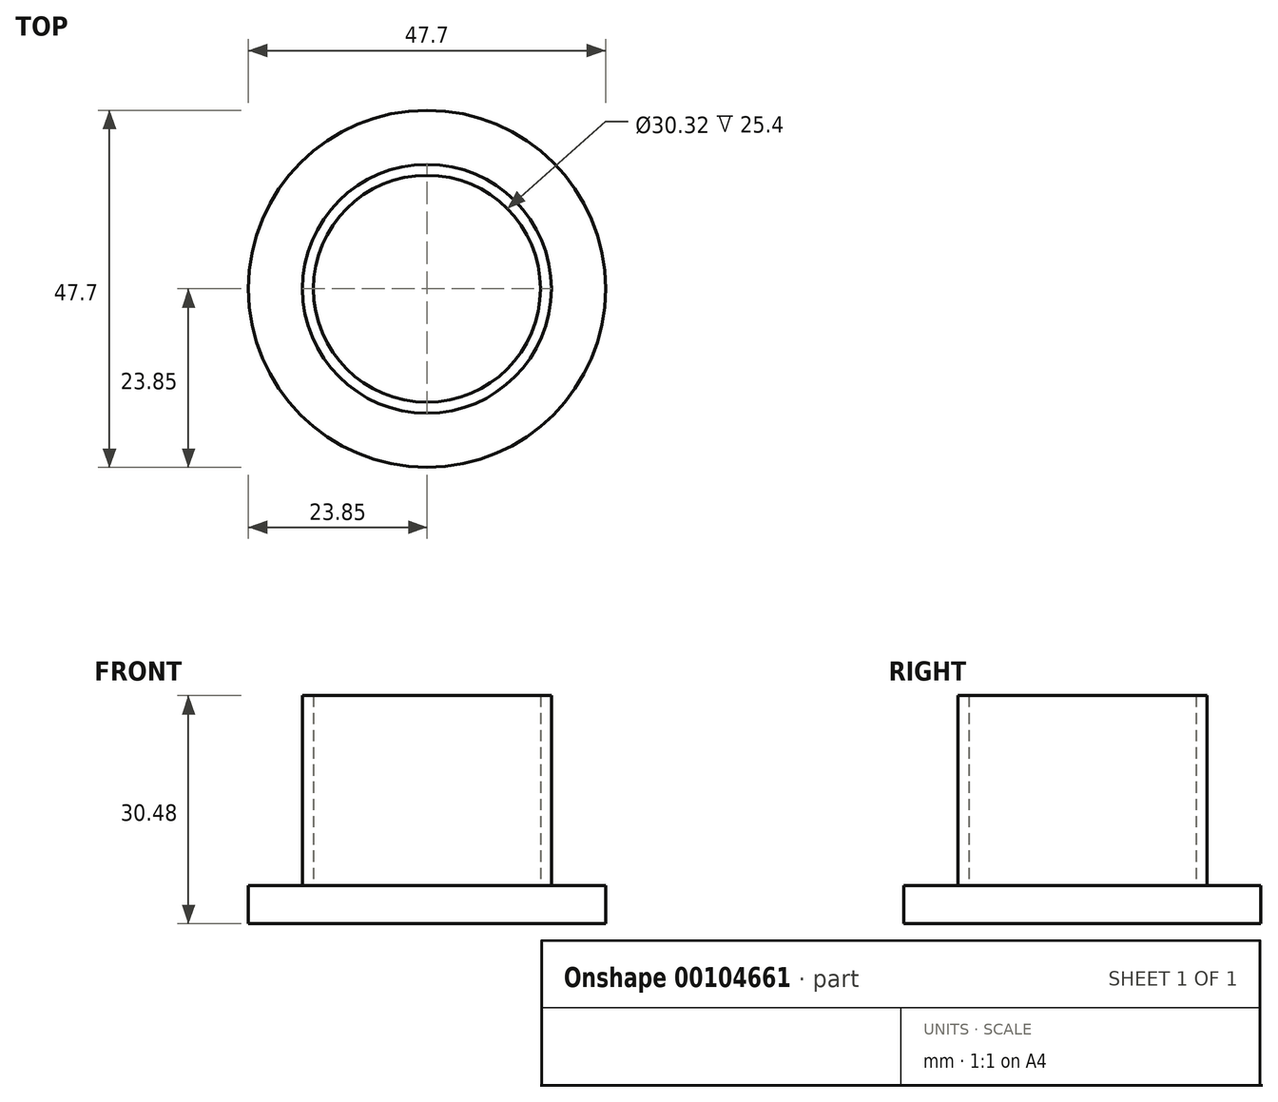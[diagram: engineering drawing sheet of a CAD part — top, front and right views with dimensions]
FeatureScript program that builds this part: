
annotation { "Feature Type Name" : "Feature", "Feature Type Description" : "" }
export const myFeature = defineFeature(function(context is Context, id is Id, definition is map)
    precondition{}
    {
        {
            var Q0;
            Q0=qCreatedBy(makeId("Top.planeOp"),FACE);
            var sketch = newSketch(context, id + "F0", { "sketchPlane" : qUnion([Q0])});
            skCircle(sketch, "E0", {"center": v(0, 0) * mm, "radius": 15.16 * mm});
            skCircle(sketch, "E1", {"center": v(0, 0) * mm, "radius": 16.63 * mm});
            skSolve(sketch);
        }
        {
            var Q0;
            Q0 = qSketchRegion(id + "F0", true);
            extrude(context, id + "F1", {"entities" : qUnion([Q0]), "depth" : 25.4 * mm});
        }
        {
            var Q0;
            Q0=qCreatedBy(makeId("Top.planeOp"),FACE);
            var sketch = newSketch(context, id + "F2", { "sketchPlane" : qUnion([Q0])});
            skCircle(sketch, "E2", {"center": v(0, 0) * mm, "radius": 23.85 * mm});
            skSolve(sketch);
        }
        {
            var Q0;
            Q0=makeQuery(id+"F2.imprint","IMPRINT",FACE,{"disambiguationData":[TD([[makeQuery(id+"F2.imprint","IMPRINT",EDGE,{"derivedFrom":sQuery(id+"F2.wireOp",EDGE,"E2")}),1.0]])]});
            extrude(context, id + "F3", {"entities" : qUnion([Q0]), "operationType" : NewBodyOperationType.ADD, "oppositeDirection" : true, "depth" : 5.08 * mm});
        }
    });
